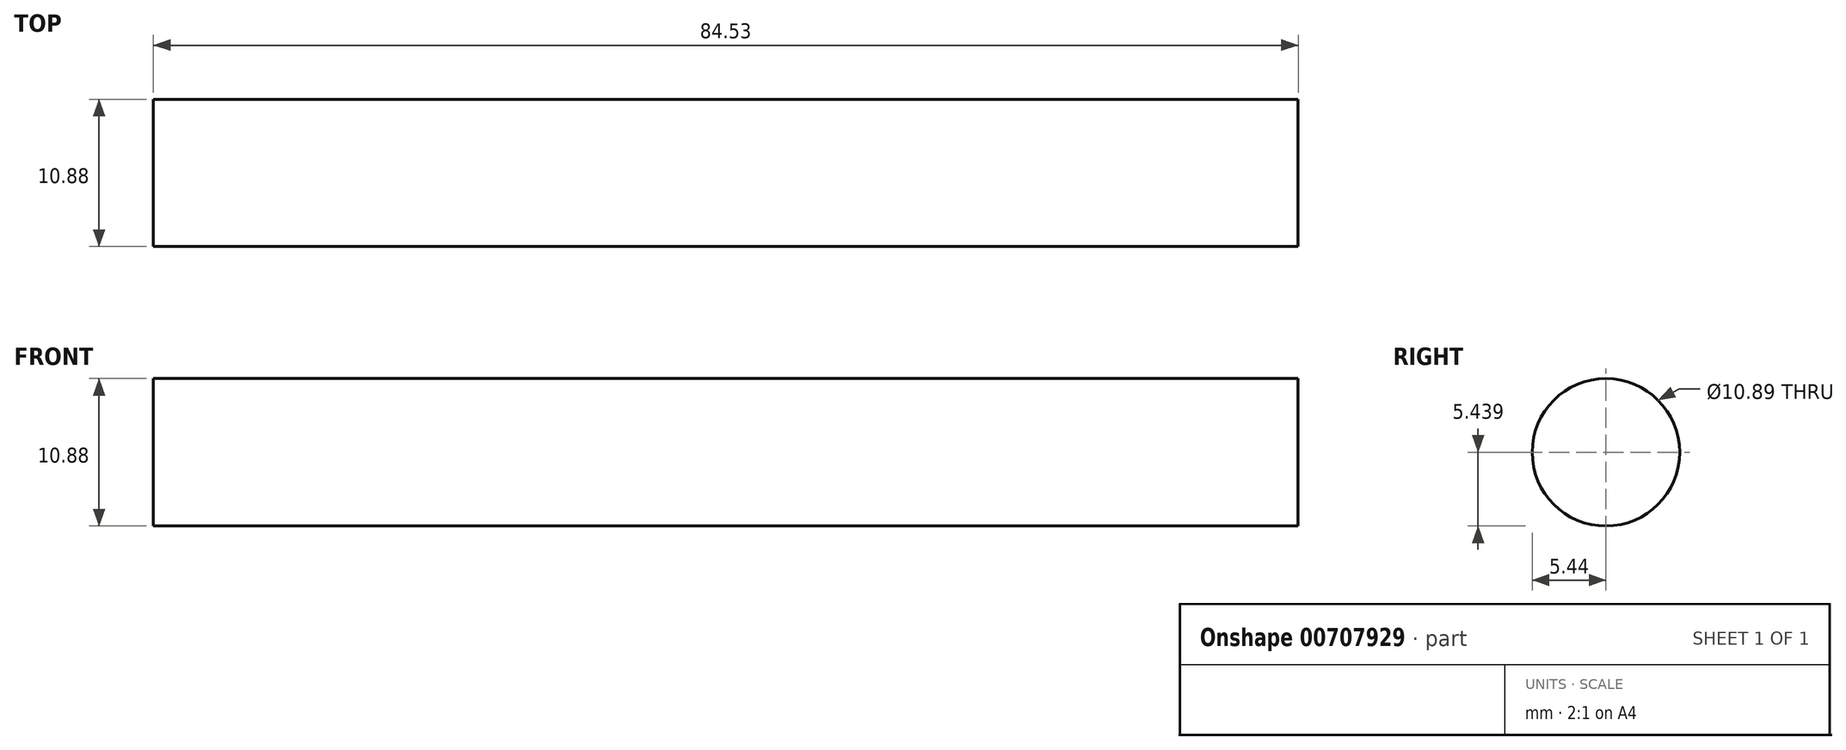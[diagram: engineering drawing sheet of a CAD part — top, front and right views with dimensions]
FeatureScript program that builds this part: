
annotation { "Feature Type Name" : "Feature", "Feature Type Description" : "" }
export const myFeature = defineFeature(function(context is Context, id is Id, definition is map)
    precondition{}
    {
        {
            var Q0;
            Q0=qCreatedBy(makeId("Front.planeOp"),FACE);
            var sketch = newSketch(context, id + "F0", { "sketchPlane" : qUnion([Q0])});
            skLineSegment(sketch, "E0", {"start": v(-107.1, 21.2) * mm, "end": v(-22.32, 21.2) * mm});
            skLineSegment(sketch, "E1", {"start": v(-107.1, 21.2) * mm, "end": v(-22.32, 21.2) * mm, "construction": true});
            skSolve(sketch);
        }
        {
            var Q0;
            Q0=qCreatedBy(makeId("Front.planeOp"),FACE);
            var sketch = newSketch(context, id + "F1", { "sketchPlane" : qUnion([Q0])});
            skLineSegment(sketch, "E2", {"start": v(-107.12, 20.44) * mm, "end": v(-22.41, 20.44) * mm});
            skSolve(sketch);
        }
        {
            var Q0;
            Q0=qCreatedBy(makeId("Front.planeOp"),FACE);
            var sketch = newSketch(context, id + "F2", { "sketchPlane" : qUnion([Q0])});
            skLineSegment(sketch, "E3", {"start": v(-106.7, 21.92) * mm, "end": v(-106.7, 15) * mm});
            skLineSegment(sketch, "E4", {"start": v(-106.7, 15) * mm, "end": v(-22.17, 15) * mm});
            skSolve(sketch);
        }
        {
            var Q0;
            Q0=sQuery(id+"F2.wireOp",EDGE,"E4");
            var Q1;
            Q1=sQuery(id+"F1.wireOp",EDGE,"E2");
            revolve(context, id + "F3", {"bodyType" : ToolBodyType.SURFACE, "surfaceOperationType" : NewSurfaceOperationType.NEW, "surfaceEntities" : qUnion([Q0]), "axis" : qUnion([Q1]), "revolveType" : RevolveType.FULL});
        }
    });
